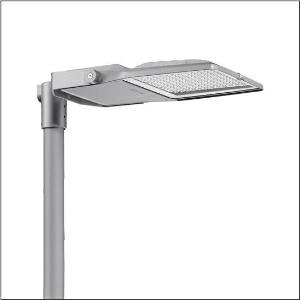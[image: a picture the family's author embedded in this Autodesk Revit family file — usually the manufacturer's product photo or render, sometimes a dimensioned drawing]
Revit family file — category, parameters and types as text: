
# Revit family: floodlight_fl_21_iq_midi___pl64_5xa7781f2e3a_9caf
name_source: partatom
category: Lighting Fixtures
units: mm (PartAtom-declared; Revit-internal decimal feet)

## family parameters
Cut with Voids When Loaded = No
Host = Face
Light Source = No
Part Type = Normal
Room Calculation Point = No
Round Connector Dimension = Use Diameter
Shared = No

## types (1)
- --- (1 x LED, 34530 lm, 270.2 W, 3000K)
    Apparent Load = 270 VA
    CIE Flux Codes = 28 80 98 100 100
    Color Rendering = 70
    Color Temperature = 3000K
    Default Elevation = 1800 mm
    Description = Floodlight FL 21 iQ midi, floodlight, primary light control with lens, of PMMA, primary optical cover: protective disc, of toughened safety glass, transparent, light distribution: PL64, light emission: direct distribution, installation type: surface-mounted, LED, High Power LED, rated luminous flux: 34.530lm, luminous efficacy: 128lm/W, light colour: 730, colour temperature: 3000K, control gear: ECG iQ, control: optimised constant luminous flux control (CLO 2.0), Desk-Remote (wireless, voltage-free reading and setting of iQ features in the workshop via application-optimized NFC function/RFID function), Light-Fading, Smart-Wire, Night-Set, Lumen-Switch, Temp-Guard, Auto-Match, with terminal, 6-pole, mains connection: 220..240V, AC, 50/60Hz, start of lifetime: 270W, end of service life: 287W, reduction: 117W, luminaire housing, of diecast aluminium, powder-coated, Siteco® metallic grey (DB 702S), corrosivity category C5 mid according to DIN EN ISO 12944, sealing non-destructively replaceable, please order mast flange separately, mast bracket, of steel, galvanised, powder-coated, Siteco® metallic grey (DB 702S), protection rating (complete): IP66, insulation class (complete): insulation class II (safety insulation), certification: CE, protection symbol: D, impact resistance: IK08, permissible operating ambient temperature: -40..+40°C, permissible operating ambient temperature for outdoor applications: -40..+50°C, standard: DIN EN 12944, LABS conformity tested according to VDMA 24364:2018-05, packaging unit: 1 piece

Light Distribution: PL64
    Height = 76 mm
    Lamp = 1 x LED
    Lamp Light Flux = 34530 lm
    Lamp Power = 270.2 W
    Lamp count = 1
    Length = 657 mm
    Luminous efficacy = 128 lm/W
    Manufacturer = Siteco
    ModVariant = No
    Model = 5XA7781F2E3A
    Number of Poles = 1
    OnlyDefault = Yes
    Power Factor = 1
    Product Name = Floodlight FL 21 iQ midi | PL64
    Product group = floodlight | pylon annexe
    ProductGroupID = 6200
    Protection Class = Protection class II
    Protection Degree = IP 66
    RLX_Detail_Level = 1
    RLX_Emergency_Light_Flux = 0 lm
    RLX_Emergency_Type = 0
    RLX_Emergency_Type_DB = No
    RlxData = <blob elided: 153597 chars, md5=447efe3e>
    Socket = socket
    Standby Power = 0 W
    System Light Flux = 34530 lm
    System Power = 270 W
    Type Comments = factory setting: luminous flux: 100 % | dim-lin: 254 | 620 mA
    Type Image = l_1007123.jpg
    URL = http://relux.com
    VarID = @adj_055153
    Voltage = 0 V
    Weight = 0.00 kg
    Width = 442 mm

## geometry (parser evidence)
native form markers: Blend x4, Sweep x14
no freeform markers — native parametric forms only
